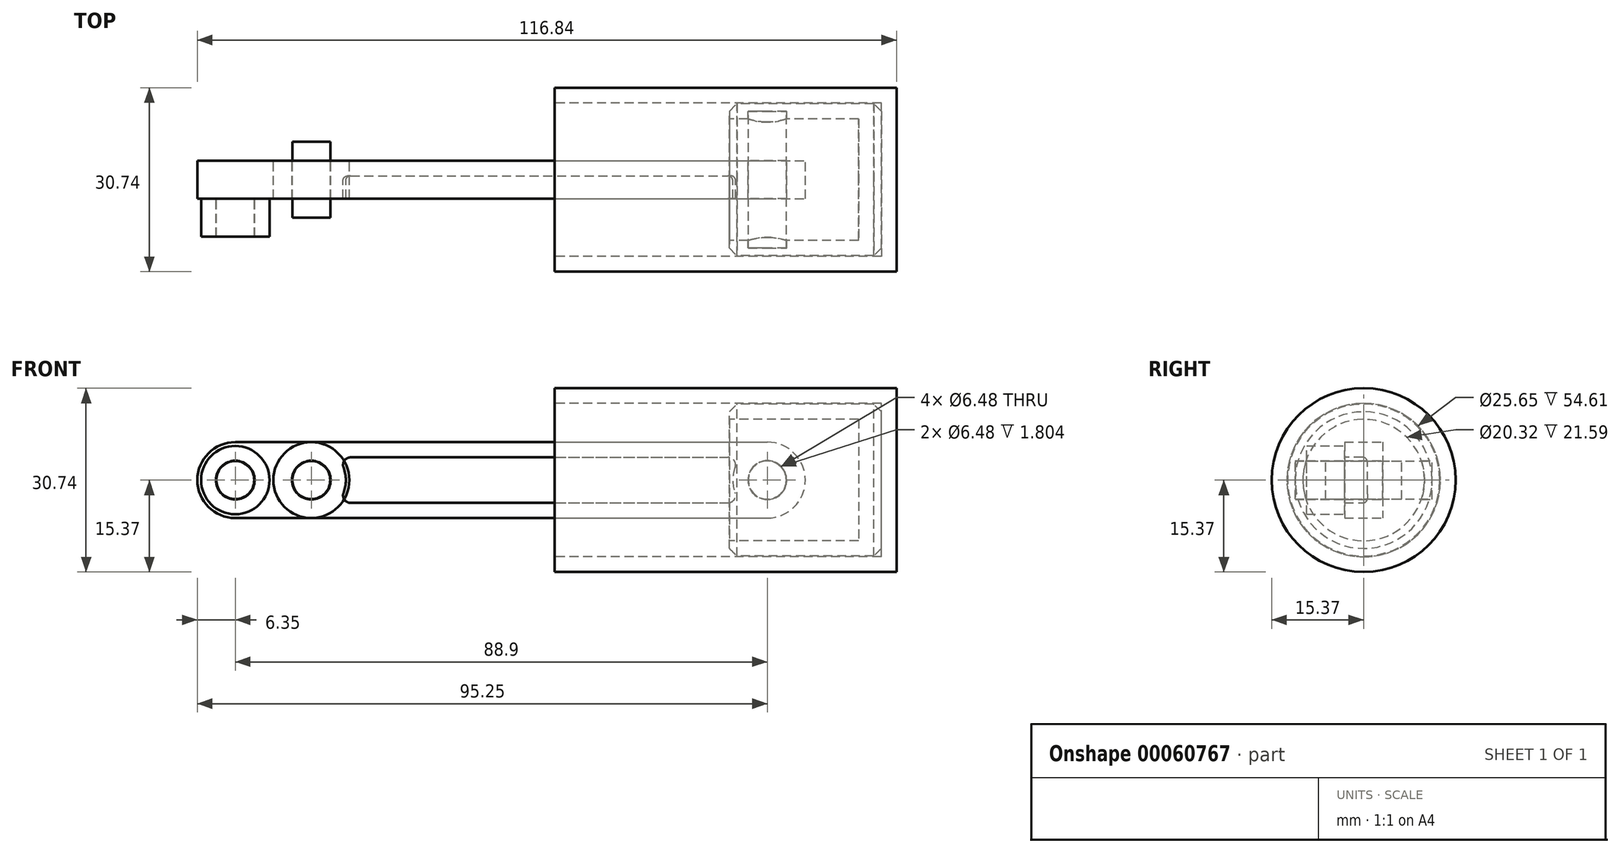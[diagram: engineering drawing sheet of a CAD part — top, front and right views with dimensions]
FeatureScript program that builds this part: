
annotation { "Feature Type Name" : "Feature", "Feature Type Description" : "" }
export const myFeature = defineFeature(function(context is Context, id is Id, definition is map)
    precondition{}
    {
        {
            var Q0;
            Q0=qCreatedBy(makeId("Front.planeOp"),FACE);
            var sketch = newSketch(context, id + "F0", { "sketchPlane" : qUnion([Q0])});
            skArc(sketch, "E0", {"start": v(0, 6.35) * mm, "mid": v(-6.35, 0) * mm, "end": v(0, -6.35) * mm});
            skArc(sketch, "E1", {"start": v(12.7, -6.35) * mm, "mid": v(19.05, 0) * mm, "end": v(12.7, 6.35) * mm});
            skLineSegment(sketch, "E2", {"start": v(0, 6.35) * mm, "end": v(12.7, 6.35) * mm});
            skLineSegment(sketch, "E3", {"start": v(12.7, -6.35) * mm, "end": v(0, -6.35) * mm});
            skCircle(sketch, "E4", {"center": v(12.7, 0) * mm, "radius": 3.24 * mm});
            skSolve(sketch);
        }
        {
            var Q0;
            Q0=qCreatedBy(makeId("Front.planeOp"),FACE);
            var sketch = newSketch(context, id + "F1", { "sketchPlane" : qUnion([Q0])});
            skArc(sketch, "E5", {"start": v(12.7, 6.35) * mm, "mid": v(6.35, 0) * mm, "end": v(12.7, -6.35) * mm});
            skArc(sketch, "E6", {"start": v(88.9, -6.35) * mm, "mid": v(95.25, 0) * mm, "end": v(88.9, 6.35) * mm});
            skLineSegment(sketch, "E7", {"start": v(12.7, 6.35) * mm, "end": v(88.9, 6.35) * mm});
            skLineSegment(sketch, "E8", {"start": v(12.7, -6.35) * mm, "end": v(88.9, -6.35) * mm});
            skCircle(sketch, "E9", {"center": v(12.7, 0) * mm, "radius": 3.24 * mm});
            skCircle(sketch, "E10", {"center": v(88.9, 0) * mm, "radius": 3.24 * mm});
            skSolve(sketch);
        }
        {
            var Q0;
            Q0=qCreatedBy(makeId("Front.planeOp"),FACE);
            var sketch = newSketch(context, id + "F2", { "sketchPlane" : qUnion([Q0])});
            skLineSegment(sketch, "E11.bottom", {"start": v(82.55, 12.7) * mm, "end": v(107.95, 12.7) * mm});
            skLineSegment(sketch, "E11.left", {"start": v(82.55, 12.7) * mm, "end": v(82.55, 10.16) * mm});
            skLineSegment(sketch, "E11.right", {"start": v(107.95, 12.7) * mm, "end": v(107.95, 0) * mm});
            skLineSegment(sketch, "E12", {"start": v(0, 0) * mm, "end": v(88.9, 0) * mm, "construction": true});
            skLineSegment(sketch, "E13", {"start": v(107.95, 0) * mm, "end": v(104.14, 0) * mm});
            skLineSegment(sketch, "E14", {"start": v(82.55, 10.16) * mm, "end": v(104.14, 10.16) * mm});
            skLineSegment(sketch, "E15", {"start": v(104.14, 10.16) * mm, "end": v(104.14, 0) * mm});
            skSolve(sketch);
        }
        {
            var Q0;
            Q0=qCreatedBy(makeId("Front.planeOp"),FACE);
            var sketch = newSketch(context, id + "F3", { "sketchPlane" : qUnion([Q0])});
            skCircle(sketch, "E16", {"center": v(12.7, 0) * mm, "radius": 3.18 * mm});
            skSolve(sketch);
        }
        {
            var Q0;
            Q0=qCreatedBy(makeId("Front.planeOp"),FACE);
            var sketch = newSketch(context, id + "F4", { "sketchPlane" : qUnion([Q0])});
            skLineSegment(sketch, "E17.bottom", {"start": v(53.34, 15.37) * mm, "end": v(110.5, 15.37) * mm});
            skLineSegment(sketch, "E17.top", {"start": v(53.34, 12.83) * mm, "end": v(110.5, 12.83) * mm});
            skLineSegment(sketch, "E17.left", {"start": v(53.34, 15.37) * mm, "end": v(53.34, 12.83) * mm});
            skLineSegment(sketch, "E17.right", {"start": v(110.5, 15.37) * mm, "end": v(110.5, 12.83) * mm});
            skSolve(sketch);
        }
        {
            var Q0;
            Q0 = qSketchRegion(id + "F4", true);
            var Q1;
            Q1=sQuery(id+"F2.wireOp",EDGE,"E12");
            revolve(context, id + "F5", {"entities" : qUnion([Q0]), "axis" : qUnion([Q1]), "revolveType" : RevolveType.FULL});
        }
        {
            var Q0;
            Q0 = qSketchRegion(id + "F3", true);
            extrude(context, id + "F6", {"entities" : qUnion([Q0]), "depth" : 12.7 * mm, "symmetric" : true});
        }
        {
            var Q0;
            Q0 = qSketchRegion(id + "F0", true);
            extrude(context, id + "F7", {"entities" : qUnion([Q0]), "depth" : 6.35 * mm, "symmetric" : true});
        }
        {
            var Q0;
            Q0 = qSketchRegion(id + "F1", true);
            extrude(context, id + "F24", {"entities" : qUnion([Q0]), "depth" : 6.35 * mm, "symmetric" : true});
        }
        {
            var Q0;
            Q0 = qSketchRegion(id + "F2", true);
            var Q1;
            Q1=sQuery(id+"F2.wireOp",EDGE,"E12");
            revolve(context, id + "F8", {"entities" : qUnion([Q0]), "axis" : qUnion([Q1]), "revolveType" : RevolveType.FULL});
        }
        {
            var Q0;
            Q0=qCreatedBy(makeId("Front.planeOp"),FACE);
            var sketch = newSketch(context, id + "F9", { "sketchPlane" : qUnion([Q0])});
            skCircle(sketch, "E18.0", {"center": v(88.9, 0) * mm, "radius": 3.24 * mm});
            skSolve(sketch);
        }
        {
            var Q0;
            Q0 = qSketchRegion(id + "F9", true);
            extrude(context, id + "F10", {"entities" : qUnion([Q0]), "depth" : 22.86 * mm, "symmetric" : true});
        }
        {
            var Q0;
            Q0=makeQuery(id+"F10.opExtrude","SWEPT_BODY",BODY,{"disambiguationData":[OSD([sQuery(id+"F9.wireOp",EDGE,"E18.0")])]});
            var Q1;
            Q1=makeQuery(id+"F8.opRevolve","SWEPT_BODY",BODY,{"disambiguationData":[OSD([sQuery(id+"F2.wireOp",EDGE,"E11.bottom"),sQuery(id+"F2.wireOp",EDGE,"E11.left"),sQuery(id+"F2.wireOp",EDGE,"E11.right"),sQuery(id+"F2.wireOp",EDGE,"E13"),sQuery(id+"F2.wireOp",EDGE,"E14"),sQuery(id+"F2.wireOp",EDGE,"E15")])]});
            booleanBodies(context, id + "F11", {"operationType" : BooleanOperationType.SUBTRACTION, "tools" : qUnion([Q0]), "targets" : qUnion([Q1])});
        }
        {
            var Q0;
            Q0=qCreatedBy(makeId("Front.planeOp"),FACE);
            var sketch = newSketch(context, id + "F12", { "sketchPlane" : qUnion([Q0])});
            skCircle(sketch, "E19", {"center": v(88.9, 0) * mm, "radius": 3.18 * mm});
            skSolve(sketch);
        }
        {
            var Q0;
            Q0 = qSketchRegion(id + "F12", true);
            extrude(context, id + "F13", {"entities" : qUnion([Q0]), "depth" : 22.86 * mm, "symmetric" : true});
        }
        {
            var Q0;
            Q0=makeQuery(id+"F8.opRevolve","SWEPT_EDGE",EDGE,{"disambiguationData":[OSD([sQuery(id+"F2.wireOp",EDGE,"E11.bottom"),sQuery(id+"F2.wireOp",EDGE,"E11.right")])]});
            var Q1;
            Q1=makeQuery(id+"F8.opRevolve","SWEPT_EDGE",EDGE,{"disambiguationData":[OSD([sQuery(id+"F2.wireOp",EDGE,"E11.bottom"),sQuery(id+"F2.wireOp",EDGE,"E11.left")])]});
            chamfer(context, id + "F14", {"entities" : qUnion([Q0, Q1]), "width" : 1.27 * mm, "tangentPropagation" : true});
        }
        {
            var Q0;
            Q0=makeQuery(id+"F24.opExtrude","CAP_FACE",FACE,{"disambiguationData":[OSD([sQuery(id+"F1.wireOp",EDGE,"E5"),sQuery(id+"F1.wireOp",EDGE,"E6"),sQuery(id+"F1.wireOp",EDGE,"E7"),sQuery(id+"F1.wireOp",EDGE,"E8"),sQuery(id+"F1.wireOp",EDGE,"E9"),sQuery(id+"F1.wireOp",EDGE,"E10")])],"isStart":false});
            shell(context, id + "F15", {"entities" : qUnion([Q0]), "thickness" : 2.54 * mm});
        }
        {
            var Q0;
            Q0=makeQuery(id+"F15.opShell","TWEAK_EDGE",EDGE,{"derivedFrom":[makeQuery(id+"F24.opExtrude","SWEPT_FACE",FACE,{"disambiguationData":[OSD([sQuery(id+"F1.wireOp",EDGE,"E7")])]}),makeQuery(id+"F24.opExtrude","SWEPT_FACE",FACE,{"disambiguationData":[OSD([sQuery(id+"F1.wireOp",EDGE,"E10")])]})]});
            var Q1;
            Q1=makeQuery(id+"F15.opShell","TWEAK_EDGE",EDGE,{"derivedFrom":[makeQuery(id+"F24.opExtrude","SWEPT_FACE",FACE,{"disambiguationData":[OSD([sQuery(id+"F1.wireOp",EDGE,"E8")])]}),makeQuery(id+"F24.opExtrude","SWEPT_FACE",FACE,{"disambiguationData":[OSD([sQuery(id+"F1.wireOp",EDGE,"E10")])]})]});
            var Q2;
            Q2=makeQuery(id+"F15.opShell","TWEAK_EDGE",EDGE,{"derivedFrom":[makeQuery(id+"F24.opExtrude","SWEPT_FACE",FACE,{"disambiguationData":[OSD([sQuery(id+"F1.wireOp",EDGE,"E7")])]}),makeQuery(id+"F24.opExtrude","SWEPT_FACE",FACE,{"disambiguationData":[OSD([sQuery(id+"F1.wireOp",EDGE,"E9")])]})]});
            var Q3;
            Q3=makeQuery(id+"F15.opShell","TWEAK_EDGE",EDGE,{"derivedFrom":[makeQuery(id+"F24.opExtrude","SWEPT_FACE",FACE,{"disambiguationData":[OSD([sQuery(id+"F1.wireOp",EDGE,"E8")])]}),makeQuery(id+"F24.opExtrude","SWEPT_FACE",FACE,{"disambiguationData":[OSD([sQuery(id+"F1.wireOp",EDGE,"E9")])]})]});
            fillet(context, id + "F16", {"entities" : qUnion([Q0, Q1, Q2, Q3]), "radius" : 1.27 * mm, "tangentPropagation" : true, "allowEdgeOverflow" : false});
        }
        {
            var Q0;
            Q0=makeQuery(id+"F15.opShell","OFFSET_FACE",FACE,{"disambiguationData":[OSD([sQuery(id+"F1.wireOp",EDGE,"E5"),sQuery(id+"F1.wireOp",EDGE,"E6"),sQuery(id+"F1.wireOp",EDGE,"E7"),sQuery(id+"F1.wireOp",EDGE,"E8"),sQuery(id+"F1.wireOp",EDGE,"E9"),sQuery(id+"F1.wireOp",EDGE,"E10")])]});
            fillet(context, id + "F17", {"entities" : qUnion([Q0]), "radius" : 0.76 * mm, "tangentPropagation" : true, "allowEdgeOverflow" : false});
        }
        {
            var Q0;
            Q0=makeQuery(id+"F7.opExtrude","CAP_FACE",FACE,{"disambiguationData":[OSD([sQuery(id+"F0.wireOp",EDGE,"E0"),sQuery(id+"F0.wireOp",EDGE,"E1"),sQuery(id+"F0.wireOp",EDGE,"E2"),sQuery(id+"F0.wireOp",EDGE,"E3"),sQuery(id+"F0.wireOp",EDGE,"E4")])],"isStart":false});
            var sketch = newSketch(context, id + "F18", { "sketchPlane" : qUnion([Q0])});
            skCircle(sketch, "E20", {"center": v(0, 0) * mm, "radius": 3.18 * mm});
            skSolve(sketch);
        }
        {
            var Q0;
            Q0 = qSketchRegion(id + "F18", true);
            extrude(context, id + "F19", {"entities" : qUnion([Q0]), "operationType" : NewBodyOperationType.ADD, "depth" : 6.35 * mm});
        }
        {
            var Q0;
            Q0=makeQuery(id+"F18.imprint","IMPRINT",FACE,{"disambiguationData":[TD([[makeQuery(id+"F18.imprint","IMPRINT",EDGE,{"derivedFrom":sQuery(id+"F18.wireOp",EDGE,"E20")}),-1.0]])]});
            var sketch = newSketch(context, id + "F20", { "sketchPlane" : qUnion([Q0])});
            skCircle(sketch, "E21", {"center": v(0, 0) * mm, "radius": 3.24 * mm});
            skCircle(sketch, "E22", {"center": v(0, 0) * mm, "radius": 5.72 * mm});
            skSolve(sketch);
        }
        {
            var Q0;
            Q0 = qSketchRegion(id + "F20", true);
            extrude(context, id + "F21", {"entities" : qUnion([Q0]), "depth" : 6.35 * mm});
        }
        {
            var Q0;
            Q0=makeQuery(id+"F5.opRevolve","SWEPT_FACE",FACE,{"disambiguationData":[OSD([sQuery(id+"F4.wireOp",EDGE,"E17.right")])]});
            var sketch = newSketch(context, id + "F22", { "sketchPlane" : qUnion([Q0])});
            skCircle(sketch, "E23.0", {"center": v(0, 0) * mm, "radius": 12.83 * mm});
            skSolve(sketch);
        }
        {
            var Q0;
            Q0 = qSketchRegion(id + "F22", true);
            extrude(context, id + "F23", {"entities" : qUnion([Q0]), "operationType" : NewBodyOperationType.ADD, "oppositeDirection" : true, "depth" : 2.54 * mm});
        }
    });
